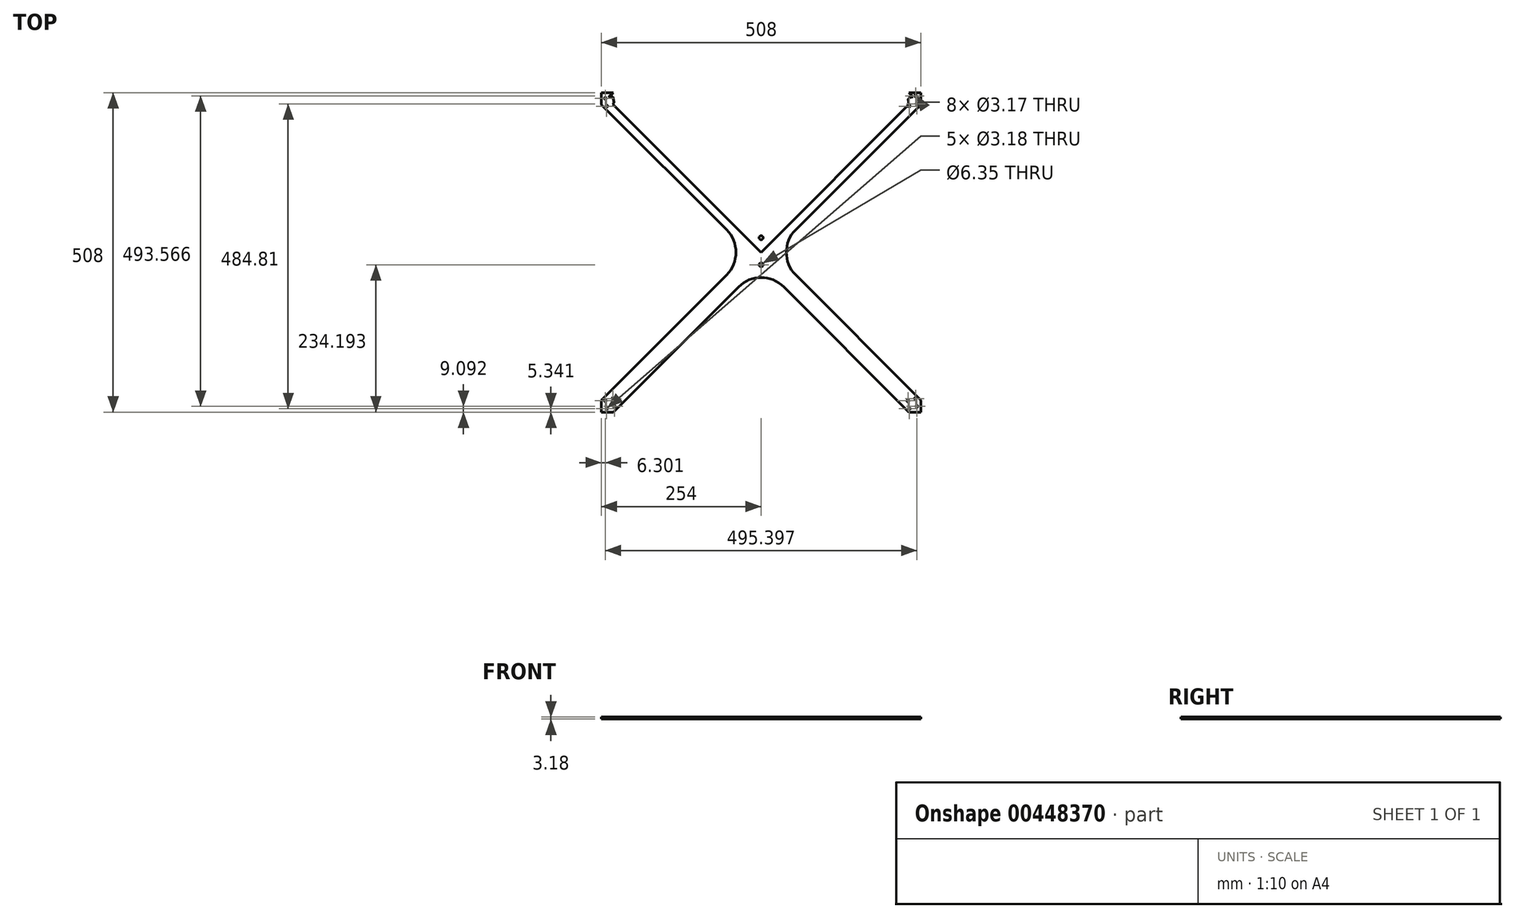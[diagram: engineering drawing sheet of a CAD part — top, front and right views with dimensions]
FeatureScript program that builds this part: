
annotation { "Feature Type Name" : "Feature", "Feature Type Description" : "" }
export const myFeature = defineFeature(function(context is Context, id is Id, definition is map)
    precondition{}
    {
        {
            var Q0;
            Q0=qCreatedBy(makeId("Top.planeOp"),FACE);
            var sketch = newSketch(context, id + "F0", { "sketchPlane" : qUnion([Q0])});
            skLineSegment(sketch, "E0.bottom", {"start": v(254, 254) * mm, "end": v(-254, 254) * mm});
            skLineSegment(sketch, "E0.top", {"start": v(254, -254) * mm, "end": v(-254, -254) * mm});
            skLineSegment(sketch, "E0.left", {"start": v(254, 254) * mm, "end": v(254, -254) * mm});
            skLineSegment(sketch, "E0.right", {"start": v(-254, 254) * mm, "end": v(-254, -254) * mm});
            skPoint(sketch, "E0.middle", {"position": v(0, 0) * mm});
            skSolve(sketch);
        }
        {
            var Q0;
            Q0=makeQuery(id+"F0.imprint","IMPRINT",FACE,{"disambiguationData":[TD([[makeQuery(id+"F0.imprint","IMPRINT",EDGE,{"derivedFrom":sQuery(id+"F0.wireOp",EDGE,"E0.bottom")}),1.0]])]});
            extrude(context, id + "F1", {"entities" : qUnion([Q0]), "depth" : 3.17 * mm});
        }
        {
            var Q0;
            Q0=makeQuery(id+"F1.opExtrude","CAP_FACE",FACE,{"disambiguationData":[OSD([sQuery(id+"F0.wireOp",EDGE,"E0.bottom"),sQuery(id+"F0.wireOp",EDGE,"E0.top"),sQuery(id+"F0.wireOp",EDGE,"E0.left"),sQuery(id+"F0.wireOp",EDGE,"E0.right")])],"isStart":false});
            var sketch = newSketch(context, id + "F2", { "sketchPlane" : qUnion([Q0])});
            skLineSegment(sketch, "E1", {"start": v(0, 19.05) * mm, "end": v(234.95, 254) * mm});
            skLineSegment(sketch, "E2", {"start": v(19.05, 0) * mm, "end": v(254, 234.95) * mm});
            skLineSegment(sketch, "E3.MirrorCS", {"start": v(0, 19.05) * mm, "end": v(-234.95, 254) * mm});
            skLineSegment(sketch, "E4.MirrorCS", {"start": v(-19.05, 0) * mm, "end": v(-254, 234.95) * mm});
            skLineSegment(sketch, "E5.MirrorCS", {"start": v(19.05, 0) * mm, "end": v(254, -234.95) * mm});
            skLineSegment(sketch, "E6.MirrorCS", {"start": v(-19.05, 0) * mm, "end": v(-254, -234.95) * mm});
            skLineSegment(sketch, "E7.MirrorCS", {"start": v(0, -19.05) * mm, "end": v(-234.95, -254) * mm});
            skLineSegment(sketch, "E8.MirrorCS", {"start": v(0, -19.05) * mm, "end": v(234.95, -254) * mm});
            skLineSegment(sketch, "E9", {"start": v(-234.95, 254) * mm, "end": v(234.95, 254) * mm});
            skLineSegment(sketch, "E10", {"start": v(254, 234.95) * mm, "end": v(254, -234.95) * mm});
            skLineSegment(sketch, "E11", {"start": v(-254, -234.95) * mm, "end": v(-254, 234.95) * mm});
            skLineSegment(sketch, "E12", {"start": v(-234.95, -254) * mm, "end": v(234.95, -254) * mm});
            skLineSegment(sketch, "E13", {"start": v(0, 0) * mm, "end": v(254, -254) * mm});
            skSolve(sketch);
        }
        {
            var Q0;
            Q0=makeQuery(id+"F2.imprint","IMPRINT",FACE,{"disambiguationData":[TD([[makeQuery(id+"F2.imprint","IMPRINT",EDGE,{"derivedFrom":sQuery(id+"F2.wireOp",EDGE,"E4.MirrorCS")}),1.0]])]});
            var Q1;
            Q1=makeQuery(id+"F2.imprint","IMPRINT",FACE,{"disambiguationData":[TD([[makeQuery(id+"F2.imprint","IMPRINT",EDGE,{"derivedFrom":sQuery(id+"F2.wireOp",EDGE,"E1")}),1.0]])]});
            var Q2;
            Q2=makeQuery(id+"F2.imprint","IMPRINT",FACE,{"disambiguationData":[TD([[makeQuery(id+"F2.imprint","IMPRINT",EDGE,{"derivedFrom":sQuery(id+"F2.wireOp",EDGE,"E2")}),-1.0]])]});
            var Q3;
            Q3=makeQuery(id+"F2.imprint","IMPRINT",FACE,{"disambiguationData":[TD([[makeQuery(id+"F2.imprint","IMPRINT",EDGE,{"derivedFrom":sQuery(id+"F2.wireOp",EDGE,"E7.MirrorCS")}),1.0]])]});
            extrude(context, id + "F3", {"entities" : qUnion([Q0, Q1, Q2, Q3]), "operationType" : NewBodyOperationType.REMOVE, "endBound" : BoundingType.THROUGH_ALL, "oppositeDirection" : true, "depth" : 25.4 * mm});
        }
        {
            var Q0;
            Q0=makeQuery(id+"F3.boolean.opBoolean","COPY",EDGE,{"derivedFrom":makeQuery(id+"F3.opExtrude","SWEPT_EDGE",EDGE,{"disambiguationData":[OSD([sQuery(id+"F2.wireOp",EDGE,"E4.MirrorCS"),sQuery(id+"F2.wireOp",EDGE,"E6.MirrorCS")])]})});
            var Q1;
            Q1=makeQuery(id+"F3.boolean.opBoolean","COPY",EDGE,{"derivedFrom":makeQuery(id+"F3.opExtrude","SWEPT_EDGE",EDGE,{"disambiguationData":[OSD([sQuery(id+"F2.wireOp",EDGE,"E7.MirrorCS"),sQuery(id+"F2.wireOp",EDGE,"E8.MirrorCS")])]})});
            var Q2;
            Q2=makeQuery(id+"F3.boolean.opBoolean","COPY",EDGE,{"derivedFrom":makeQuery(id+"F3.opExtrude","SWEPT_EDGE",EDGE,{"disambiguationData":[OSD([sQuery(id+"F2.wireOp",EDGE,"E2"),sQuery(id+"F2.wireOp",EDGE,"E5.MirrorCS")])]})});
            var Q3;
            Q3=makeQuery(id+"F3.boolean.opBoolean","COPY",EDGE,{"derivedFrom":makeQuery(id+"F3.opExtrude","SWEPT_EDGE",EDGE,{"disambiguationData":[OSD([sQuery(id+"F2.wireOp",EDGE,"E1"),sQuery(id+"F2.wireOp",EDGE,"E3.MirrorCS")])]})});
            fillet(context, id + "F4", {"entities" : qUnion([Q0, Q1, Q2, Q3]), "radius" : 50.8 * mm, "tangentPropagation" : true, "allowEdgeOverflow" : false});
        }
        {
            var Q0;
            Q0=makeQuery(id+"F1.opExtrude","CAP_FACE",FACE,{"disambiguationData":[OSD([sQuery(id+"F0.wireOp",EDGE,"E0.bottom"),sQuery(id+"F0.wireOp",EDGE,"E0.top"),sQuery(id+"F0.wireOp",EDGE,"E0.left"),sQuery(id+"F0.wireOp",EDGE,"E0.right")])],"isStart":true});
            var sketch = newSketch(context, id + "F5", { "sketchPlane" : qUnion([Q0])});
            skLineSegment(sketch, "E14", {"start": v(-40.1, 0) * mm, "end": v(40.1, 0) * mm});
            skLineSegment(sketch, "E15", {"start": v(0, 40.1) * mm, "end": v(0, -40.1) * mm});
            skLineSegment(sketch, "E16", {"start": v(0, 0) * mm, "end": v(-254, -254) * mm});
            skLineSegment(sketch, "E17", {"start": v(0, 0) * mm, "end": v(254, -254) * mm});
            skLineSegment(sketch, "E18", {"start": v(0, 0) * mm, "end": v(254, 254) * mm});
            skLineSegment(sketch, "E19", {"start": v(234.95, -254) * mm, "end": v(254, -234.95) * mm});
            skLineSegment(sketch, "E20", {"start": v(-254, -234.95) * mm, "end": v(-234.95, -254) * mm});
            skLineSegment(sketch, "E21", {"start": v(234.95, 254) * mm, "end": v(254, 234.95) * mm});
            skLineSegment(sketch, "E22", {"start": v(-254, 234.95) * mm, "end": v(-234.95, 254) * mm});
            skCircle(sketch, "E23", {"center": v(247.7, -236.15) * mm, "radius": 1.59 * mm});
            skCircle(sketch, "E24", {"center": v(-125.31, -108.96) * mm, "radius": 1.59 * mm});
            skCircle(sketch, "E25", {"center": v(235.57, -232.4) * mm, "radius": 1.59 * mm});
            skCircle(sketch, "E26", {"center": v(245.5, -248.66) * mm, "radius": 1.59 * mm});
            skCircle(sketch, "E27", {"center": v(233.36, -244.9) * mm, "radius": 1.59 * mm});
            skLineSegment(sketch, "E28", {"start": v(247.7, -236.15) * mm, "end": v(235.57, -232.4) * mm});
            skLineSegment(sketch, "E29", {"start": v(247.7, -236.15) * mm, "end": v(245.5, -248.66) * mm});
            skLineSegment(sketch, "E30", {"start": v(235.57, -232.4) * mm, "end": v(233.36, -244.9) * mm});
            skLineSegment(sketch, "E31", {"start": v(233.36, -244.9) * mm, "end": v(245.5, -248.66) * mm});
            skLineSegment(sketch, "E32", {"start": v(245.5, -248.66) * mm, "end": v(235.57, -232.4) * mm});
            skPoint(sketch, "E33.endSnap0", {"position": v(240.53, -240.53) * mm});
            skCircle(sketch, "E34", {"center": v(-233.36, -236.15) * mm, "radius": 1.59 * mm});
            skCircle(sketch, "E35", {"center": v(-245.5, -232.4) * mm, "radius": 1.59 * mm});
            skCircle(sketch, "E36", {"center": v(-235.57, -248.66) * mm, "radius": 1.59 * mm});
            skCircle(sketch, "E37", {"center": v(-247.7, -244.9) * mm, "radius": 1.59 * mm});
            skLineSegment(sketch, "E38", {"start": v(-233.36, -236.15) * mm, "end": v(-245.5, -232.4) * mm});
            skLineSegment(sketch, "E39", {"start": v(-233.36, -236.15) * mm, "end": v(-235.57, -248.66) * mm});
            skLineSegment(sketch, "E40", {"start": v(-245.5, -232.4) * mm, "end": v(-247.7, -244.9) * mm});
            skLineSegment(sketch, "E41", {"start": v(-247.7, -244.9) * mm, "end": v(-235.57, -248.66) * mm});
            skLineSegment(sketch, "E42", {"start": v(-235.57, -248.66) * mm, "end": v(-245.5, -232.4) * mm});
            skPoint(sketch, "E43.endSnap0", {"position": v(-240.53, -240.53) * mm});
            skCircle(sketch, "E44", {"center": v(247.7, 244.9) * mm, "radius": 1.59 * mm});
            skCircle(sketch, "E45", {"center": v(235.57, 248.66) * mm, "radius": 1.59 * mm});
            skCircle(sketch, "E46", {"center": v(245.5, 232.4) * mm, "radius": 1.59 * mm});
            skCircle(sketch, "E47", {"center": v(233.36, 236.15) * mm, "radius": 1.59 * mm});
            skLineSegment(sketch, "E48", {"start": v(247.7, 244.9) * mm, "end": v(235.57, 248.66) * mm});
            skLineSegment(sketch, "E49", {"start": v(247.7, 244.9) * mm, "end": v(245.5, 232.4) * mm});
            skLineSegment(sketch, "E50", {"start": v(235.57, 248.66) * mm, "end": v(233.36, 236.15) * mm});
            skLineSegment(sketch, "E51", {"start": v(233.36, 236.15) * mm, "end": v(245.5, 232.4) * mm});
            skLineSegment(sketch, "E52", {"start": v(245.5, 232.4) * mm, "end": v(235.57, 248.66) * mm});
            skPoint(sketch, "E53.endSnap0", {"position": v(240.53, 240.53) * mm});
            skCircle(sketch, "E54", {"center": v(-233.36, 244.9) * mm, "radius": 1.59 * mm});
            skCircle(sketch, "E55", {"center": v(-245.5, 248.66) * mm, "radius": 1.59 * mm});
            skCircle(sketch, "E56", {"center": v(-235.57, 232.4) * mm, "radius": 1.59 * mm});
            skCircle(sketch, "E57", {"center": v(-247.7, 236.15) * mm, "radius": 1.59 * mm});
            skLineSegment(sketch, "E58", {"start": v(-233.36, 244.9) * mm, "end": v(-245.5, 248.66) * mm});
            skLineSegment(sketch, "E59", {"start": v(-233.36, 244.9) * mm, "end": v(-235.57, 232.4) * mm});
            skLineSegment(sketch, "E60", {"start": v(-245.5, 248.66) * mm, "end": v(-247.7, 236.15) * mm});
            skLineSegment(sketch, "E61", {"start": v(-247.7, 236.15) * mm, "end": v(-235.57, 232.4) * mm});
            skLineSegment(sketch, "E62", {"start": v(-235.57, 232.4) * mm, "end": v(-245.5, 248.66) * mm});
            skPoint(sketch, "E63.endSnap0", {"position": v(-240.53, 240.53) * mm});
            skLineSegment(sketch, "E64", {"start": v(-254, 254) * mm, "end": v(0, 0) * mm});
            skCircle(sketch, "E65", {"center": v(0, -23.16) * mm, "radius": 3.18 * mm});
            skCircle(sketch, "E66", {"center": v(0, 19.8) * mm, "radius": 3.18 * mm});
            skSolve(sketch);
        }
        {
            var Q0;
            {var subQ0=sQuery(id+"F5.wireOp",EDGE,"E42");var subQ1=sQuery(id+"F5.wireOp",EDGE,"E36");var subQ2=makeQuery(id+"F5.imprint","INTERSECT",VERTEX,{"derivedFrom":[subQ1,subQ0]});Q0=makeQuery(id+"F5.imprint","IMPRINT",FACE,{"disambiguationData":[TD([[makeQuery(id+"F5.imprint","IMPRINT",EDGE,{"disambiguationData":[TD([[subQ2,1.0]])],"derivedFrom":subQ1}),1.0]])]});}
            var Q1;
            {var subQ0=sQuery(id+"F5.wireOp",EDGE,"E42");var subQ1=sQuery(id+"F5.wireOp",EDGE,"E36");var subQ2=makeQuery(id+"F5.imprint","INTERSECT",VERTEX,{"derivedFrom":[subQ1,subQ0]});Q1=makeQuery(id+"F5.imprint","IMPRINT",FACE,{"disambiguationData":[TD([[makeQuery(id+"F5.imprint","IMPRINT",EDGE,{"disambiguationData":[TD([[subQ2,-1.0]])],"derivedFrom":subQ1}),1.0]])]});}
            var Q2;
            {var subQ0=sQuery(id+"F5.wireOp",EDGE,"E39");var subQ1=sQuery(id+"F5.wireOp",EDGE,"E36");var subQ2=makeQuery(id+"F5.imprint","INTERSECT",VERTEX,{"derivedFrom":[subQ1,subQ0]});Q2=makeQuery(id+"F5.imprint","IMPRINT",FACE,{"disambiguationData":[TD([[makeQuery(id+"F5.imprint","IMPRINT",EDGE,{"disambiguationData":[TD([[subQ2,1.0]])],"derivedFrom":subQ1}),1.0]])]});}
            var Q3;
            {var subQ0=sQuery(id+"F5.wireOp",EDGE,"E40");var subQ1=sQuery(id+"F5.wireOp",EDGE,"E37");var subQ2=makeQuery(id+"F5.imprint","INTERSECT",VERTEX,{"derivedFrom":[subQ1,subQ0]});Q3=makeQuery(id+"F5.imprint","IMPRINT",FACE,{"disambiguationData":[TD([[makeQuery(id+"F5.imprint","IMPRINT",EDGE,{"disambiguationData":[TD([[subQ2,-1.0]])],"derivedFrom":subQ1}),1.0]])]});}
            var Q4;
            {var subQ0=sQuery(id+"F5.wireOp",EDGE,"E42");var subQ1=sQuery(id+"F5.wireOp",EDGE,"E35");var subQ2=makeQuery(id+"F5.imprint","INTERSECT",VERTEX,{"derivedFrom":[subQ1,subQ0]});Q4=makeQuery(id+"F5.imprint","IMPRINT",FACE,{"disambiguationData":[TD([[makeQuery(id+"F5.imprint","IMPRINT",EDGE,{"disambiguationData":[TD([[subQ2,-1.0]])],"derivedFrom":subQ1}),1.0]])]});}
            var Q5;
            {var subQ0=sQuery(id+"F5.wireOp",EDGE,"E42");var subQ1=sQuery(id+"F5.wireOp",EDGE,"E35");var subQ2=makeQuery(id+"F5.imprint","INTERSECT",VERTEX,{"derivedFrom":[subQ1,subQ0]});Q5=makeQuery(id+"F5.imprint","IMPRINT",FACE,{"disambiguationData":[TD([[makeQuery(id+"F5.imprint","IMPRINT",EDGE,{"disambiguationData":[TD([[subQ2,1.0]])],"derivedFrom":subQ1}),1.0]])]});}
            var Q6;
            {var subQ0=sQuery(id+"F5.wireOp",EDGE,"E40");var subQ1=sQuery(id+"F5.wireOp",EDGE,"E35");var subQ2=makeQuery(id+"F5.imprint","INTERSECT",VERTEX,{"derivedFrom":[subQ1,subQ0]});Q6=makeQuery(id+"F5.imprint","IMPRINT",FACE,{"disambiguationData":[TD([[makeQuery(id+"F5.imprint","IMPRINT",EDGE,{"disambiguationData":[TD([[subQ2,1.0]])],"derivedFrom":subQ1}),1.0]])]});}
            var Q7;
            {var subQ0=sQuery(id+"F5.wireOp",EDGE,"E38");var subQ1=sQuery(id+"F5.wireOp",EDGE,"E34");var subQ2=makeQuery(id+"F5.imprint","INTERSECT",VERTEX,{"derivedFrom":[subQ1,subQ0]});Q7=makeQuery(id+"F5.imprint","IMPRINT",FACE,{"disambiguationData":[TD([[makeQuery(id+"F5.imprint","IMPRINT",EDGE,{"disambiguationData":[TD([[subQ2,1.0]])],"derivedFrom":subQ1}),1.0]])]});}
            var Q8;
            {var subQ0=sQuery(id+"F5.wireOp",EDGE,"E38");var subQ1=sQuery(id+"F5.wireOp",EDGE,"E34");var subQ2=makeQuery(id+"F5.imprint","INTERSECT",VERTEX,{"derivedFrom":[subQ1,subQ0]});Q8=makeQuery(id+"F5.imprint","IMPRINT",FACE,{"disambiguationData":[TD([[makeQuery(id+"F5.imprint","IMPRINT",EDGE,{"disambiguationData":[TD([[subQ2,-1.0]])],"derivedFrom":subQ1}),1.0]])]});}
            var Q9;
            {var subQ0=sQuery(id+"F5.wireOp",EDGE,"E40");var subQ1=sQuery(id+"F5.wireOp",EDGE,"E37");var subQ2=makeQuery(id+"F5.imprint","INTERSECT",VERTEX,{"derivedFrom":[subQ1,subQ0]});Q9=makeQuery(id+"F5.imprint","IMPRINT",FACE,{"disambiguationData":[TD([[makeQuery(id+"F5.imprint","IMPRINT",EDGE,{"disambiguationData":[TD([[subQ2,1.0]])],"derivedFrom":subQ1}),1.0]])]});}
            var Q10;
            {var subQ0=sQuery(id+"F5.wireOp",EDGE,"E58");var subQ1=sQuery(id+"F5.wireOp",EDGE,"E54");var subQ2=makeQuery(id+"F5.imprint","INTERSECT",VERTEX,{"derivedFrom":[subQ1,subQ0]});Q10=makeQuery(id+"F5.imprint","IMPRINT",FACE,{"disambiguationData":[TD([[makeQuery(id+"F5.imprint","IMPRINT",EDGE,{"disambiguationData":[TD([[subQ2,1.0]])],"derivedFrom":subQ1}),1.0]])]});}
            var Q11;
            {var subQ0=sQuery(id+"F5.wireOp",EDGE,"E58");var subQ1=sQuery(id+"F5.wireOp",EDGE,"E54");var subQ2=makeQuery(id+"F5.imprint","INTERSECT",VERTEX,{"derivedFrom":[subQ1,subQ0]});Q11=makeQuery(id+"F5.imprint","IMPRINT",FACE,{"disambiguationData":[TD([[makeQuery(id+"F5.imprint","IMPRINT",EDGE,{"disambiguationData":[TD([[subQ2,-1.0]])],"derivedFrom":subQ1}),1.0]])]});}
            var Q12;
            {var subQ0=sQuery(id+"F5.wireOp",EDGE,"E62");var subQ1=sQuery(id+"F5.wireOp",EDGE,"E55");var subQ2=makeQuery(id+"F5.imprint","INTERSECT",VERTEX,{"derivedFrom":[subQ1,subQ0]});Q12=makeQuery(id+"F5.imprint","IMPRINT",FACE,{"disambiguationData":[TD([[makeQuery(id+"F5.imprint","IMPRINT",EDGE,{"disambiguationData":[TD([[subQ2,-1.0]])],"derivedFrom":subQ1}),1.0]])]});}
            var Q13;
            {var subQ0=sQuery(id+"F5.wireOp",EDGE,"E62");var subQ1=sQuery(id+"F5.wireOp",EDGE,"E55");var subQ2=makeQuery(id+"F5.imprint","INTERSECT",VERTEX,{"derivedFrom":[subQ1,subQ0]});Q13=makeQuery(id+"F5.imprint","IMPRINT",FACE,{"disambiguationData":[TD([[makeQuery(id+"F5.imprint","IMPRINT",EDGE,{"disambiguationData":[TD([[subQ2,1.0]])],"derivedFrom":subQ1}),1.0]])]});}
            var Q14;
            {var subQ0=sQuery(id+"F5.wireOp",EDGE,"E60");var subQ1=sQuery(id+"F5.wireOp",EDGE,"E55");var subQ2=makeQuery(id+"F5.imprint","INTERSECT",VERTEX,{"derivedFrom":[subQ1,subQ0]});Q14=makeQuery(id+"F5.imprint","IMPRINT",FACE,{"disambiguationData":[TD([[makeQuery(id+"F5.imprint","IMPRINT",EDGE,{"disambiguationData":[TD([[subQ2,1.0]])],"derivedFrom":subQ1}),1.0]])]});}
            var Q15;
            {var subQ0=sQuery(id+"F5.wireOp",EDGE,"E60");var subQ1=sQuery(id+"F5.wireOp",EDGE,"E57");var subQ2=makeQuery(id+"F5.imprint","INTERSECT",VERTEX,{"derivedFrom":[subQ1,subQ0]});Q15=makeQuery(id+"F5.imprint","IMPRINT",FACE,{"disambiguationData":[TD([[makeQuery(id+"F5.imprint","IMPRINT",EDGE,{"disambiguationData":[TD([[subQ2,1.0]])],"derivedFrom":subQ1}),1.0]])]});}
            var Q16;
            {var subQ0=sQuery(id+"F5.wireOp",EDGE,"E60");var subQ1=sQuery(id+"F5.wireOp",EDGE,"E57");var subQ2=makeQuery(id+"F5.imprint","INTERSECT",VERTEX,{"derivedFrom":[subQ1,subQ0]});Q16=makeQuery(id+"F5.imprint","IMPRINT",FACE,{"disambiguationData":[TD([[makeQuery(id+"F5.imprint","IMPRINT",EDGE,{"disambiguationData":[TD([[subQ2,-1.0]])],"derivedFrom":subQ1}),1.0]])]});}
            var Q17;
            {var subQ0=sQuery(id+"F5.wireOp",EDGE,"E59");var subQ1=sQuery(id+"F5.wireOp",EDGE,"E56");var subQ2=makeQuery(id+"F5.imprint","INTERSECT",VERTEX,{"derivedFrom":[subQ1,subQ0]});Q17=makeQuery(id+"F5.imprint","IMPRINT",FACE,{"disambiguationData":[TD([[makeQuery(id+"F5.imprint","IMPRINT",EDGE,{"disambiguationData":[TD([[subQ2,1.0]])],"derivedFrom":subQ1}),1.0]])]});}
            var Q18;
            {var subQ0=sQuery(id+"F5.wireOp",EDGE,"E62");var subQ1=sQuery(id+"F5.wireOp",EDGE,"E56");var subQ2=makeQuery(id+"F5.imprint","INTERSECT",VERTEX,{"derivedFrom":[subQ1,subQ0]});Q18=makeQuery(id+"F5.imprint","IMPRINT",FACE,{"disambiguationData":[TD([[makeQuery(id+"F5.imprint","IMPRINT",EDGE,{"disambiguationData":[TD([[subQ2,1.0]])],"derivedFrom":subQ1}),1.0]])]});}
            var Q19;
            {var subQ0=sQuery(id+"F5.wireOp",EDGE,"E62");var subQ1=sQuery(id+"F5.wireOp",EDGE,"E56");var subQ2=makeQuery(id+"F5.imprint","INTERSECT",VERTEX,{"derivedFrom":[subQ1,subQ0]});Q19=makeQuery(id+"F5.imprint","IMPRINT",FACE,{"disambiguationData":[TD([[makeQuery(id+"F5.imprint","IMPRINT",EDGE,{"disambiguationData":[TD([[subQ2,-1.0]])],"derivedFrom":subQ1}),1.0]])]});}
            var Q20;
            {var subQ0=sQuery(id+"F5.wireOp",EDGE,"E48");var subQ1=sQuery(id+"F5.wireOp",EDGE,"E44");var subQ2=makeQuery(id+"F5.imprint","INTERSECT",VERTEX,{"derivedFrom":[subQ1,subQ0]});Q20=makeQuery(id+"F5.imprint","IMPRINT",FACE,{"disambiguationData":[TD([[makeQuery(id+"F5.imprint","IMPRINT",EDGE,{"disambiguationData":[TD([[subQ2,1.0]])],"derivedFrom":subQ1}),1.0]])]});}
            var Q21;
            {var subQ0=sQuery(id+"F5.wireOp",EDGE,"E48");var subQ1=sQuery(id+"F5.wireOp",EDGE,"E44");var subQ2=makeQuery(id+"F5.imprint","INTERSECT",VERTEX,{"derivedFrom":[subQ1,subQ0]});Q21=makeQuery(id+"F5.imprint","IMPRINT",FACE,{"disambiguationData":[TD([[makeQuery(id+"F5.imprint","IMPRINT",EDGE,{"disambiguationData":[TD([[subQ2,-1.0]])],"derivedFrom":subQ1}),1.0]])]});}
            var Q22;
            {var subQ0=sQuery(id+"F5.wireOp",EDGE,"E52");var subQ1=sQuery(id+"F5.wireOp",EDGE,"E46");var subQ2=makeQuery(id+"F5.imprint","INTERSECT",VERTEX,{"derivedFrom":[subQ1,subQ0]});Q22=makeQuery(id+"F5.imprint","IMPRINT",FACE,{"disambiguationData":[TD([[makeQuery(id+"F5.imprint","IMPRINT",EDGE,{"disambiguationData":[TD([[subQ2,1.0]])],"derivedFrom":subQ1}),1.0]])]});}
            var Q23;
            {var subQ0=sQuery(id+"F5.wireOp",EDGE,"E49");var subQ1=sQuery(id+"F5.wireOp",EDGE,"E46");var subQ2=makeQuery(id+"F5.imprint","INTERSECT",VERTEX,{"derivedFrom":[subQ1,subQ0]});Q23=makeQuery(id+"F5.imprint","IMPRINT",FACE,{"disambiguationData":[TD([[makeQuery(id+"F5.imprint","IMPRINT",EDGE,{"disambiguationData":[TD([[subQ2,1.0]])],"derivedFrom":subQ1}),1.0]])]});}
            var Q24;
            {var subQ0=sQuery(id+"F5.wireOp",EDGE,"E52");var subQ1=sQuery(id+"F5.wireOp",EDGE,"E46");var subQ2=makeQuery(id+"F5.imprint","INTERSECT",VERTEX,{"derivedFrom":[subQ1,subQ0]});Q24=makeQuery(id+"F5.imprint","IMPRINT",FACE,{"disambiguationData":[TD([[makeQuery(id+"F5.imprint","IMPRINT",EDGE,{"disambiguationData":[TD([[subQ2,-1.0]])],"derivedFrom":subQ1}),1.0]])]});}
            var Q25;
            {var subQ0=sQuery(id+"F5.wireOp",EDGE,"E50");var subQ1=sQuery(id+"F5.wireOp",EDGE,"E47");var subQ2=makeQuery(id+"F5.imprint","INTERSECT",VERTEX,{"derivedFrom":[subQ1,subQ0]});Q25=makeQuery(id+"F5.imprint","IMPRINT",FACE,{"disambiguationData":[TD([[makeQuery(id+"F5.imprint","IMPRINT",EDGE,{"disambiguationData":[TD([[subQ2,-1.0]])],"derivedFrom":subQ1}),1.0]])]});}
            var Q26;
            {var subQ0=sQuery(id+"F5.wireOp",EDGE,"E50");var subQ1=sQuery(id+"F5.wireOp",EDGE,"E47");var subQ2=makeQuery(id+"F5.imprint","INTERSECT",VERTEX,{"derivedFrom":[subQ1,subQ0]});Q26=makeQuery(id+"F5.imprint","IMPRINT",FACE,{"disambiguationData":[TD([[makeQuery(id+"F5.imprint","IMPRINT",EDGE,{"disambiguationData":[TD([[subQ2,1.0]])],"derivedFrom":subQ1}),1.0]])]});}
            var Q27;
            {var subQ0=sQuery(id+"F5.wireOp",EDGE,"E52");var subQ1=sQuery(id+"F5.wireOp",EDGE,"E45");var subQ2=makeQuery(id+"F5.imprint","INTERSECT",VERTEX,{"derivedFrom":[subQ1,subQ0]});Q27=makeQuery(id+"F5.imprint","IMPRINT",FACE,{"disambiguationData":[TD([[makeQuery(id+"F5.imprint","IMPRINT",EDGE,{"disambiguationData":[TD([[subQ2,1.0]])],"derivedFrom":subQ1}),1.0]])]});}
            var Q28;
            {var subQ0=sQuery(id+"F5.wireOp",EDGE,"E52");var subQ1=sQuery(id+"F5.wireOp",EDGE,"E45");var subQ2=makeQuery(id+"F5.imprint","INTERSECT",VERTEX,{"derivedFrom":[subQ1,subQ0]});Q28=makeQuery(id+"F5.imprint","IMPRINT",FACE,{"disambiguationData":[TD([[makeQuery(id+"F5.imprint","IMPRINT",EDGE,{"disambiguationData":[TD([[subQ2,-1.0]])],"derivedFrom":subQ1}),1.0]])]});}
            var Q29;
            {var subQ0=sQuery(id+"F5.wireOp",EDGE,"E50");var subQ1=sQuery(id+"F5.wireOp",EDGE,"E45");var subQ2=makeQuery(id+"F5.imprint","INTERSECT",VERTEX,{"derivedFrom":[subQ1,subQ0]});Q29=makeQuery(id+"F5.imprint","IMPRINT",FACE,{"disambiguationData":[TD([[makeQuery(id+"F5.imprint","IMPRINT",EDGE,{"disambiguationData":[TD([[subQ2,1.0]])],"derivedFrom":subQ1}),1.0]])]});}
            var Q30;
            {var subQ0=sQuery(id+"F5.wireOp",EDGE,"E29");var subQ1=sQuery(id+"F5.wireOp",EDGE,"E26");var subQ2=makeQuery(id+"F5.imprint","INTERSECT",VERTEX,{"derivedFrom":[subQ1,subQ0]});Q30=makeQuery(id+"F5.imprint","IMPRINT",FACE,{"disambiguationData":[TD([[makeQuery(id+"F5.imprint","IMPRINT",EDGE,{"disambiguationData":[TD([[subQ2,1.0]])],"derivedFrom":subQ1}),1.0]])]});}
            var Q31;
            {var subQ0=sQuery(id+"F5.wireOp",EDGE,"E32");var subQ1=sQuery(id+"F5.wireOp",EDGE,"E26");var subQ2=makeQuery(id+"F5.imprint","INTERSECT",VERTEX,{"derivedFrom":[subQ1,subQ0]});Q31=makeQuery(id+"F5.imprint","IMPRINT",FACE,{"disambiguationData":[TD([[makeQuery(id+"F5.imprint","IMPRINT",EDGE,{"disambiguationData":[TD([[subQ2,-1.0]])],"derivedFrom":subQ1}),1.0]])]});}
            var Q32;
            {var subQ0=sQuery(id+"F5.wireOp",EDGE,"E32");var subQ1=sQuery(id+"F5.wireOp",EDGE,"E26");var subQ2=makeQuery(id+"F5.imprint","INTERSECT",VERTEX,{"derivedFrom":[subQ1,subQ0]});Q32=makeQuery(id+"F5.imprint","IMPRINT",FACE,{"disambiguationData":[TD([[makeQuery(id+"F5.imprint","IMPRINT",EDGE,{"disambiguationData":[TD([[subQ2,1.0]])],"derivedFrom":subQ1}),1.0]])]});}
            var Q33;
            {var subQ0=sQuery(id+"F5.wireOp",EDGE,"E30");var subQ1=sQuery(id+"F5.wireOp",EDGE,"E27");var subQ2=makeQuery(id+"F5.imprint","INTERSECT",VERTEX,{"derivedFrom":[subQ1,subQ0]});Q33=makeQuery(id+"F5.imprint","IMPRINT",FACE,{"disambiguationData":[TD([[makeQuery(id+"F5.imprint","IMPRINT",EDGE,{"disambiguationData":[TD([[subQ2,1.0]])],"derivedFrom":subQ1}),1.0]])]});}
            var Q34;
            {var subQ0=sQuery(id+"F5.wireOp",EDGE,"E30");var subQ1=sQuery(id+"F5.wireOp",EDGE,"E27");var subQ2=makeQuery(id+"F5.imprint","INTERSECT",VERTEX,{"derivedFrom":[subQ1,subQ0]});Q34=makeQuery(id+"F5.imprint","IMPRINT",FACE,{"disambiguationData":[TD([[makeQuery(id+"F5.imprint","IMPRINT",EDGE,{"disambiguationData":[TD([[subQ2,-1.0]])],"derivedFrom":subQ1}),1.0]])]});}
            var Q35;
            {var subQ0=sQuery(id+"F5.wireOp",EDGE,"E32");var subQ1=sQuery(id+"F5.wireOp",EDGE,"E25");var subQ2=makeQuery(id+"F5.imprint","INTERSECT",VERTEX,{"derivedFrom":[subQ1,subQ0]});Q35=makeQuery(id+"F5.imprint","IMPRINT",FACE,{"disambiguationData":[TD([[makeQuery(id+"F5.imprint","IMPRINT",EDGE,{"disambiguationData":[TD([[subQ2,1.0]])],"derivedFrom":subQ1}),1.0]])]});}
            var Q36;
            {var subQ0=sQuery(id+"F5.wireOp",EDGE,"E32");var subQ1=sQuery(id+"F5.wireOp",EDGE,"E25");var subQ2=makeQuery(id+"F5.imprint","INTERSECT",VERTEX,{"derivedFrom":[subQ1,subQ0]});Q36=makeQuery(id+"F5.imprint","IMPRINT",FACE,{"disambiguationData":[TD([[makeQuery(id+"F5.imprint","IMPRINT",EDGE,{"disambiguationData":[TD([[subQ2,-1.0]])],"derivedFrom":subQ1}),1.0]])]});}
            var Q37;
            {var subQ0=sQuery(id+"F5.wireOp",EDGE,"E30");var subQ1=sQuery(id+"F5.wireOp",EDGE,"E25");var subQ2=makeQuery(id+"F5.imprint","INTERSECT",VERTEX,{"derivedFrom":[subQ1,subQ0]});Q37=makeQuery(id+"F5.imprint","IMPRINT",FACE,{"disambiguationData":[TD([[makeQuery(id+"F5.imprint","IMPRINT",EDGE,{"disambiguationData":[TD([[subQ2,1.0]])],"derivedFrom":subQ1}),1.0]])]});}
            var Q38;
            {var subQ0=sQuery(id+"F5.wireOp",EDGE,"E28");var subQ1=sQuery(id+"F5.wireOp",EDGE,"E23");var subQ2=makeQuery(id+"F5.imprint","INTERSECT",VERTEX,{"derivedFrom":[subQ1,subQ0]});Q38=makeQuery(id+"F5.imprint","IMPRINT",FACE,{"disambiguationData":[TD([[makeQuery(id+"F5.imprint","IMPRINT",EDGE,{"disambiguationData":[TD([[subQ2,-1.0]])],"derivedFrom":subQ1}),1.0]])]});}
            var Q39;
            {var subQ0=sQuery(id+"F5.wireOp",EDGE,"E28");var subQ1=sQuery(id+"F5.wireOp",EDGE,"E23");var subQ2=makeQuery(id+"F5.imprint","INTERSECT",VERTEX,{"derivedFrom":[subQ1,subQ0]});Q39=makeQuery(id+"F5.imprint","IMPRINT",FACE,{"disambiguationData":[TD([[makeQuery(id+"F5.imprint","IMPRINT",EDGE,{"disambiguationData":[TD([[subQ2,1.0]])],"derivedFrom":subQ1}),1.0]])]});}
            var Q40;
            {var subQ0=sQuery(id+"F5.wireOp",EDGE,"E66");var subQ1=sQuery(id+"F5.wireOp",EDGE,"E15");var subQ2=makeQuery(id+"F5.imprint","INTERSECT",VERTEX,{"disambiguationData":[OD(0.0)],"derivedFrom":[subQ1,subQ0]});Q40=makeQuery(id+"F5.imprint","IMPRINT",FACE,{"disambiguationData":[TD([[makeQuery(id+"F5.imprint","IMPRINT",EDGE,{"disambiguationData":[TD([[subQ2,-1.0]])],"derivedFrom":subQ1}),1.0]])]});}
            var Q41;
            {var subQ0=sQuery(id+"F5.wireOp",EDGE,"E65");var subQ1=sQuery(id+"F5.wireOp",EDGE,"E15");var subQ2=makeQuery(id+"F5.imprint","INTERSECT",VERTEX,{"disambiguationData":[OD(0.0)],"derivedFrom":[subQ1,subQ0]});Q41=makeQuery(id+"F5.imprint","IMPRINT",FACE,{"disambiguationData":[TD([[makeQuery(id+"F5.imprint","IMPRINT",EDGE,{"disambiguationData":[TD([[subQ2,-1.0]])],"derivedFrom":subQ1}),-1.0]])]});}
            var Q42;
            {var subQ0=sQuery(id+"F5.wireOp",EDGE,"E65");var subQ1=sQuery(id+"F5.wireOp",EDGE,"E15");var subQ2=makeQuery(id+"F5.imprint","INTERSECT",VERTEX,{"disambiguationData":[OD(0.0)],"derivedFrom":[subQ1,subQ0]});Q42=makeQuery(id+"F5.imprint","IMPRINT",FACE,{"disambiguationData":[TD([[makeQuery(id+"F5.imprint","IMPRINT",EDGE,{"disambiguationData":[TD([[subQ2,-1.0]])],"derivedFrom":subQ1}),1.0]])]});}
            var Q43;
            {var subQ0=sQuery(id+"F5.wireOp",EDGE,"E66");var subQ1=sQuery(id+"F5.wireOp",EDGE,"E15");var subQ2=makeQuery(id+"F5.imprint","INTERSECT",VERTEX,{"disambiguationData":[OD(0.0)],"derivedFrom":[subQ1,subQ0]});Q43=makeQuery(id+"F5.imprint","IMPRINT",FACE,{"disambiguationData":[TD([[makeQuery(id+"F5.imprint","IMPRINT",EDGE,{"disambiguationData":[TD([[subQ2,-1.0]])],"derivedFrom":subQ1}),-1.0]])]});}
            extrude(context, id + "F6", {"entities" : qUnion([Q0, Q1, Q2, Q3, Q4, Q5, Q6, Q7, Q8, Q9, Q10, Q11, Q12, Q13, Q14, Q15, Q16, Q17, Q18, Q19, Q20, Q21, Q22, Q23, Q24, Q25, Q26, Q27, Q28, Q29, Q30, Q31, Q32, Q33, Q34, Q35, Q36, Q37, Q38, Q39, Q40, Q41, Q42, Q43]), "operationType" : NewBodyOperationType.REMOVE, "endBound" : BoundingType.THROUGH_ALL, "oppositeDirection" : true, "depth" : 25.4 * mm});
        }
    });
